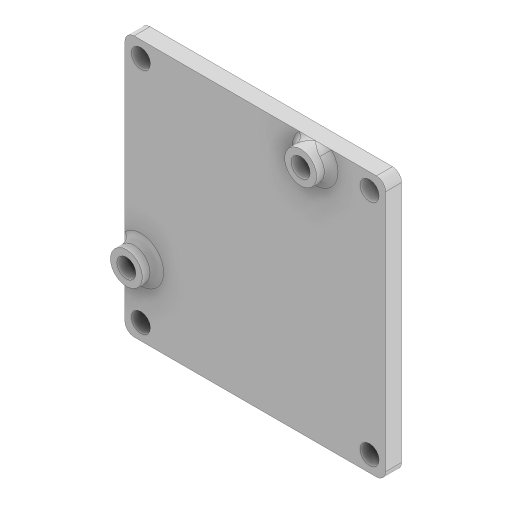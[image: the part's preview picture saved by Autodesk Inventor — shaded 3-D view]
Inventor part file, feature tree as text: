
AUTODESK INVENTOR PART (.ipt)
format: ipt  version: 2023 (Build 270158000, 158)  size: 178,176 bytes
history: native  units: mm
features: sketch x2, extrude x2, fillet x2
ambient origin geometry x8: Origin, YZ Plane, XZ Plane, XY Plane, X Axis, Y Axis, Z Axis, Center Point
bodies: Solid1 (feature_tree)
feature tree (6):
  sketch  "Sketch1"  dims[d0=57.0mm d1=57.0mm]
  extrude  "Extrusion1"  Depth=57.0mm
  extrude  "Extrusion2"  Depth=2.0mm
  sketch  "Sketch Driven Pattern1"  dims[d2=50.0mm d3=50.0mm d4=4.15mm d5=4.15mm d6=4.15mm d7=4.15mm d8=38.1mm d9=38.1mm d10=4.15mm d12=4.15mm d13=7.0mm d14=3.5mm d15=0.0mm d16=3.175mm d17=0.0mm d19=1.5mm d20=2.0mm]
  fillet  "Fillet2"  Radius=4.15mm
  fillet  "Fillet3"  Radius=4.15mm
